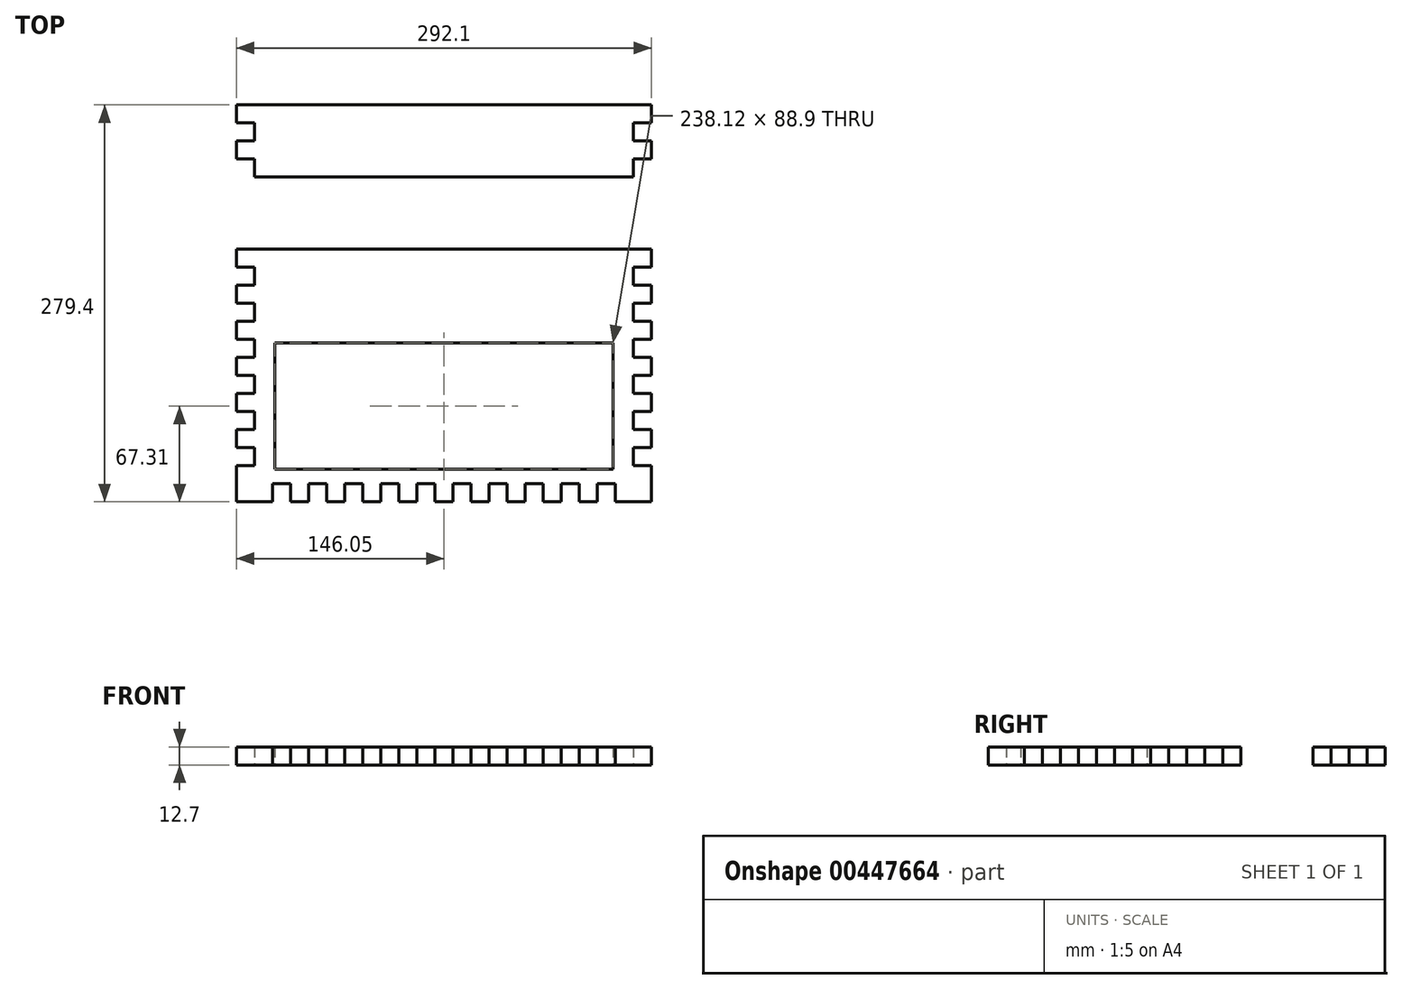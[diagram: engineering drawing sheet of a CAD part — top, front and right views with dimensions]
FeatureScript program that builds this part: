
annotation { "Feature Type Name" : "Feature", "Feature Type Description" : "" }
export const myFeature = defineFeature(function(context is Context, id is Id, definition is map)
    precondition{}
    {
        {
            var Q0;
            Q0=qCreatedBy(makeId("Top.planeOp"),FACE);
            var sketch = newSketch(context, id + "F0", { "sketchPlane" : qUnion([Q0])});
            skLineSegment(sketch, "E0.bottom", {"start": v(0, 0) * mm, "end": v(292.1, 0) * mm});
            skLineSegment(sketch, "E0.top", {"start": v(0, -177.8) * mm, "end": v(25.4, -177.8) * mm});
            skLineSegment(sketch, "E0.left", {"start": v(0, 0) * mm, "end": v(0, -12.7) * mm});
            skLineSegment(sketch, "E1", {"start": v(0, -12.7) * mm, "end": v(12.7, -12.7) * mm});
            skLineSegment(sketch, "E2", {"start": v(12.7, -12.7) * mm, "end": v(12.7, -25.4) * mm});
            skLineSegment(sketch, "E3", {"start": v(12.7, -25.4) * mm, "end": v(0, -25.4) * mm});
            skLineSegment(sketch, "E4", {"start": v(0, -25.4) * mm, "end": v(0, -38.1) * mm});
            skLineSegment(sketch, "E5", {"start": v(0, -38.1) * mm, "end": v(12.7, -38.1) * mm});
            skLineSegment(sketch, "E6", {"start": v(12.7, -38.1) * mm, "end": v(12.7, -50.8) * mm});
            skLineSegment(sketch, "E7", {"start": v(12.7, -50.8) * mm, "end": v(0, -50.8) * mm});
            skLineSegment(sketch, "E8", {"start": v(0, -50.8) * mm, "end": v(0, -63.5) * mm});
            skLineSegment(sketch, "E9", {"start": v(0, -63.5) * mm, "end": v(12.7, -63.5) * mm});
            skLineSegment(sketch, "E10", {"start": v(12.7, -63.5) * mm, "end": v(12.7, -76.2) * mm});
            skLineSegment(sketch, "E11", {"start": v(12.7, -76.2) * mm, "end": v(0, -76.2) * mm});
            skLineSegment(sketch, "E12", {"start": v(0, -76.2) * mm, "end": v(0, -88.9) * mm});
            skLineSegment(sketch, "E13", {"start": v(0, -88.9) * mm, "end": v(12.7, -88.9) * mm});
            skLineSegment(sketch, "E14", {"start": v(12.7, -88.9) * mm, "end": v(12.7, -101.6) * mm});
            skLineSegment(sketch, "E15", {"start": v(12.7, -101.6) * mm, "end": v(0, -101.6) * mm});
            skLineSegment(sketch, "E16.trimOffspring", {"start": v(0, -101.6) * mm, "end": v(0, -114.3) * mm});
            skLineSegment(sketch, "E17", {"start": v(0, -114.3) * mm, "end": v(12.7, -114.3) * mm});
            skLineSegment(sketch, "E18", {"start": v(12.7, -114.3) * mm, "end": v(12.7, -127) * mm});
            skLineSegment(sketch, "E19", {"start": v(12.7, -127) * mm, "end": v(0, -127) * mm});
            skLineSegment(sketch, "E20", {"start": v(0, -127) * mm, "end": v(0, -139.7) * mm});
            skLineSegment(sketch, "E21", {"start": v(0, -139.7) * mm, "end": v(12.7, -139.7) * mm});
            skLineSegment(sketch, "E22", {"start": v(12.7, -139.7) * mm, "end": v(12.7, -152.4) * mm});
            skLineSegment(sketch, "E23", {"start": v(12.7, -152.4) * mm, "end": v(0, -152.4) * mm});
            skLineSegment(sketch, "E24.trimOffspring", {"start": v(0, -152.4) * mm, "end": v(0, -177.8) * mm});
            skLineSegment(sketch, "E25", {"start": v(146.05, 0) * mm, "end": v(146.05, -172) * mm, "construction": true});
            skLineSegment(sketch, "E26.MirrorCS", {"start": v(292.1, 0) * mm, "end": v(292.1, -12.7) * mm});
            skLineSegment(sketch, "E27.MirrorCS", {"start": v(292.1, -12.7) * mm, "end": v(279.4, -12.7) * mm});
            skLineSegment(sketch, "E28.MirrorCS", {"start": v(279.4, -12.7) * mm, "end": v(279.4, -25.4) * mm});
            skLineSegment(sketch, "E29.MirrorCS", {"start": v(279.4, -25.4) * mm, "end": v(292.1, -25.4) * mm});
            skLineSegment(sketch, "E30.MirrorCS", {"start": v(292.1, -25.4) * mm, "end": v(292.1, -38.1) * mm});
            skLineSegment(sketch, "E31.MirrorCS", {"start": v(292.1, -38.1) * mm, "end": v(279.4, -38.1) * mm});
            skLineSegment(sketch, "E32.MirrorCS", {"start": v(279.4, -38.1) * mm, "end": v(279.4, -50.8) * mm});
            skLineSegment(sketch, "E33.MirrorCS", {"start": v(279.4, -50.8) * mm, "end": v(292.1, -50.8) * mm});
            skLineSegment(sketch, "E34.MirrorCS", {"start": v(292.1, -50.8) * mm, "end": v(292.1, -63.5) * mm});
            skLineSegment(sketch, "E35.MirrorCS", {"start": v(292.1, -63.5) * mm, "end": v(279.4, -63.5) * mm});
            skLineSegment(sketch, "E36.MirrorCS", {"start": v(279.4, -63.5) * mm, "end": v(279.4, -76.2) * mm});
            skLineSegment(sketch, "E37.MirrorCS", {"start": v(279.4, -76.2) * mm, "end": v(292.1, -76.2) * mm});
            skLineSegment(sketch, "E38.MirrorCS", {"start": v(292.1, -76.2) * mm, "end": v(292.1, -88.9) * mm});
            skLineSegment(sketch, "E39.MirrorCS", {"start": v(292.1, -88.9) * mm, "end": v(279.4, -88.9) * mm});
            skLineSegment(sketch, "E40.MirrorCS", {"start": v(279.4, -88.9) * mm, "end": v(279.4, -101.6) * mm});
            skLineSegment(sketch, "E41.MirrorCS", {"start": v(279.4, -101.6) * mm, "end": v(292.1, -101.6) * mm});
            skLineSegment(sketch, "E42.MirrorCS", {"start": v(292.1, -101.6) * mm, "end": v(292.1, -114.3) * mm});
            skLineSegment(sketch, "E43.MirrorCS", {"start": v(292.1, -114.3) * mm, "end": v(279.4, -114.3) * mm});
            skLineSegment(sketch, "E44.MirrorCS", {"start": v(279.4, -114.3) * mm, "end": v(279.4, -127) * mm});
            skLineSegment(sketch, "E45.MirrorCS", {"start": v(279.4, -127) * mm, "end": v(292.1, -127) * mm});
            skLineSegment(sketch, "E46.MirrorCS", {"start": v(292.1, -127) * mm, "end": v(292.1, -139.7) * mm});
            skLineSegment(sketch, "E47.MirrorCS", {"start": v(292.1, -139.7) * mm, "end": v(279.4, -139.7) * mm});
            skLineSegment(sketch, "E48.MirrorCS", {"start": v(279.4, -139.7) * mm, "end": v(279.4, -152.4) * mm});
            skLineSegment(sketch, "E49.MirrorCS", {"start": v(279.4, -152.4) * mm, "end": v(292.1, -152.4) * mm});
            skLineSegment(sketch, "E50.MirrorCS", {"start": v(292.1, -152.4) * mm, "end": v(292.1, -177.8) * mm});
            skLineSegment(sketch, "E51", {"start": v(25.4, -177.8) * mm, "end": v(25.4, -165.1) * mm});
            skLineSegment(sketch, "E52", {"start": v(25.4, -165.1) * mm, "end": v(38.1, -165.1) * mm});
            skLineSegment(sketch, "E53", {"start": v(38.1, -165.1) * mm, "end": v(38.1, -177.8) * mm});
            skLineSegment(sketch, "E54", {"start": v(38.1, -177.8) * mm, "end": v(50.8, -177.8) * mm});
            skLineSegment(sketch, "E55", {"start": v(50.8, -177.8) * mm, "end": v(50.8, -165.1) * mm});
            skLineSegment(sketch, "E56", {"start": v(50.8, -165.1) * mm, "end": v(63.5, -165.1) * mm});
            skLineSegment(sketch, "E57", {"start": v(63.5, -165.1) * mm, "end": v(63.5, -177.8) * mm});
            skLineSegment(sketch, "E58", {"start": v(63.5, -177.8) * mm, "end": v(76.2, -177.8) * mm});
            skLineSegment(sketch, "E59", {"start": v(76.2, -177.8) * mm, "end": v(76.2, -165.1) * mm});
            skLineSegment(sketch, "E60", {"start": v(76.2, -165.1) * mm, "end": v(88.9, -165.1) * mm});
            skLineSegment(sketch, "E61", {"start": v(88.9, -165.1) * mm, "end": v(88.9, -177.8) * mm});
            skLineSegment(sketch, "E62", {"start": v(88.9, -177.8) * mm, "end": v(101.6, -177.8) * mm});
            skLineSegment(sketch, "E63", {"start": v(101.6, -177.8) * mm, "end": v(101.6, -165.1) * mm});
            skLineSegment(sketch, "E64", {"start": v(101.6, -165.1) * mm, "end": v(114.3, -165.1) * mm});
            skLineSegment(sketch, "E65", {"start": v(114.3, -165.1) * mm, "end": v(114.3, -177.8) * mm});
            skLineSegment(sketch, "E66", {"start": v(114.3, -177.8) * mm, "end": v(127, -177.8) * mm});
            skLineSegment(sketch, "E67", {"start": v(127, -177.8) * mm, "end": v(127, -165.1) * mm});
            skLineSegment(sketch, "E68", {"start": v(127, -165.1) * mm, "end": v(139.7, -165.1) * mm});
            skLineSegment(sketch, "E69", {"start": v(139.7, -165.1) * mm, "end": v(139.7, -177.8) * mm});
            skLineSegment(sketch, "E70.trimOffspring", {"start": v(139.7, -177.8) * mm, "end": v(152.4, -177.8) * mm});
            skLineSegment(sketch, "E71", {"start": v(152.4, -177.8) * mm, "end": v(152.4, -165.1) * mm});
            skLineSegment(sketch, "E72", {"start": v(152.4, -165.1) * mm, "end": v(165.1, -165.1) * mm});
            skLineSegment(sketch, "E73", {"start": v(165.1, -165.1) * mm, "end": v(165.1, -177.8) * mm});
            skLineSegment(sketch, "E74", {"start": v(165.1, -177.8) * mm, "end": v(177.8, -177.8) * mm});
            skLineSegment(sketch, "E75", {"start": v(177.8, -177.8) * mm, "end": v(177.8, -165.1) * mm});
            skLineSegment(sketch, "E76", {"start": v(177.8, -165.1) * mm, "end": v(190.5, -165.1) * mm});
            skLineSegment(sketch, "E77", {"start": v(190.5, -165.1) * mm, "end": v(190.5, -177.8) * mm});
            skLineSegment(sketch, "E78", {"start": v(190.5, -177.8) * mm, "end": v(203.2, -177.8) * mm});
            skLineSegment(sketch, "E79", {"start": v(203.2, -177.8) * mm, "end": v(203.2, -165.1) * mm});
            skLineSegment(sketch, "E80", {"start": v(203.2, -165.1) * mm, "end": v(215.9, -165.1) * mm});
            skLineSegment(sketch, "E81", {"start": v(215.9, -165.1) * mm, "end": v(215.9, -177.8) * mm});
            skLineSegment(sketch, "E82.trimOffspring", {"start": v(215.9, -177.8) * mm, "end": v(228.6, -177.8) * mm});
            skLineSegment(sketch, "E83", {"start": v(228.6, -177.8) * mm, "end": v(228.6, -165.1) * mm});
            skLineSegment(sketch, "E84", {"start": v(228.6, -165.1) * mm, "end": v(241.3, -165.1) * mm});
            skLineSegment(sketch, "E85", {"start": v(241.3, -165.1) * mm, "end": v(241.3, -177.8) * mm});
            skLineSegment(sketch, "E86", {"start": v(241.3, -177.8) * mm, "end": v(254, -177.8) * mm});
            skLineSegment(sketch, "E87", {"start": v(254, -177.8) * mm, "end": v(254, -165.1) * mm});
            skLineSegment(sketch, "E88", {"start": v(254, -165.1) * mm, "end": v(266.7, -165.1) * mm});
            skLineSegment(sketch, "E89", {"start": v(266.7, -165.1) * mm, "end": v(266.7, -177.8) * mm});
            skLineSegment(sketch, "E90.trimOffspring", {"start": v(266.7, -177.8) * mm, "end": v(292.1, -177.8) * mm});
            skLineSegment(sketch, "E91.bottom", {"start": v(26.99, -66.04) * mm, "end": v(265.11, -66.04) * mm});
            skLineSegment(sketch, "E91.top", {"start": v(26.99, -154.94) * mm, "end": v(265.11, -154.94) * mm});
            skLineSegment(sketch, "E91.left", {"start": v(26.99, -66.04) * mm, "end": v(26.99, -154.94) * mm});
            skLineSegment(sketch, "E91.right", {"start": v(265.11, -66.04) * mm, "end": v(265.11, -154.94) * mm});
            skLineSegment(sketch, "E92.bottom", {"start": v(0, 101.6) * mm, "end": v(292.1, 101.6) * mm});
            skLineSegment(sketch, "E92.top", {"start": v(12.7, 50.8) * mm, "end": v(279.4, 50.8) * mm});
            skLineSegment(sketch, "E92.left", {"start": v(0, 101.6) * mm, "end": v(0, 88.9) * mm});
            skLineSegment(sketch, "E93", {"start": v(0, 63.5) * mm, "end": v(12.7, 63.5) * mm});
            skLineSegment(sketch, "E94", {"start": v(12.7, 63.5) * mm, "end": v(12.7, 50.8) * mm});
            skLineSegment(sketch, "E95", {"start": v(0, 63.5) * mm, "end": v(0, 76.2) * mm});
            skLineSegment(sketch, "E96", {"start": v(0, 76.2) * mm, "end": v(12.7, 76.2) * mm});
            skLineSegment(sketch, "E97", {"start": v(12.7, 76.2) * mm, "end": v(12.7, 88.9) * mm});
            skLineSegment(sketch, "E98", {"start": v(12.7, 88.9) * mm, "end": v(0, 88.9) * mm});
            skLineSegment(sketch, "E99.trimOffspring", {"start": v(0, 76.2) * mm, "end": v(0, 63.5) * mm});
            skLineSegment(sketch, "E100", {"start": v(146.05, 101.6) * mm, "end": v(146.05, 50.8) * mm, "construction": true});
            skLineSegment(sketch, "E101.MirrorCS", {"start": v(292.1, 101.6) * mm, "end": v(292.1, 88.9) * mm});
            skLineSegment(sketch, "E102.MirrorCS", {"start": v(279.4, 76.2) * mm, "end": v(279.4, 88.9) * mm});
            skLineSegment(sketch, "E103.MirrorCS", {"start": v(292.1, 76.2) * mm, "end": v(279.4, 76.2) * mm});
            skLineSegment(sketch, "E104.MirrorCS", {"start": v(292.1, 76.2) * mm, "end": v(292.1, 63.5) * mm});
            skLineSegment(sketch, "E105.MirrorCS", {"start": v(292.1, 63.5) * mm, "end": v(279.4, 63.5) * mm});
            skLineSegment(sketch, "E106.MirrorCS", {"start": v(279.4, 63.5) * mm, "end": v(279.4, 50.8) * mm});
            skLineSegment(sketch, "E107.MirrorCS", {"start": v(279.4, 88.9) * mm, "end": v(292.1, 88.9) * mm});
            skSolve(sketch);
        }
        {
            var Q0;
            Q0 = qSketchRegion(id + "F0", true);
            extrude(context, id + "F1", {"entities" : qUnion([Q0]), "depth" : 12.7 * mm});
        }
    });
